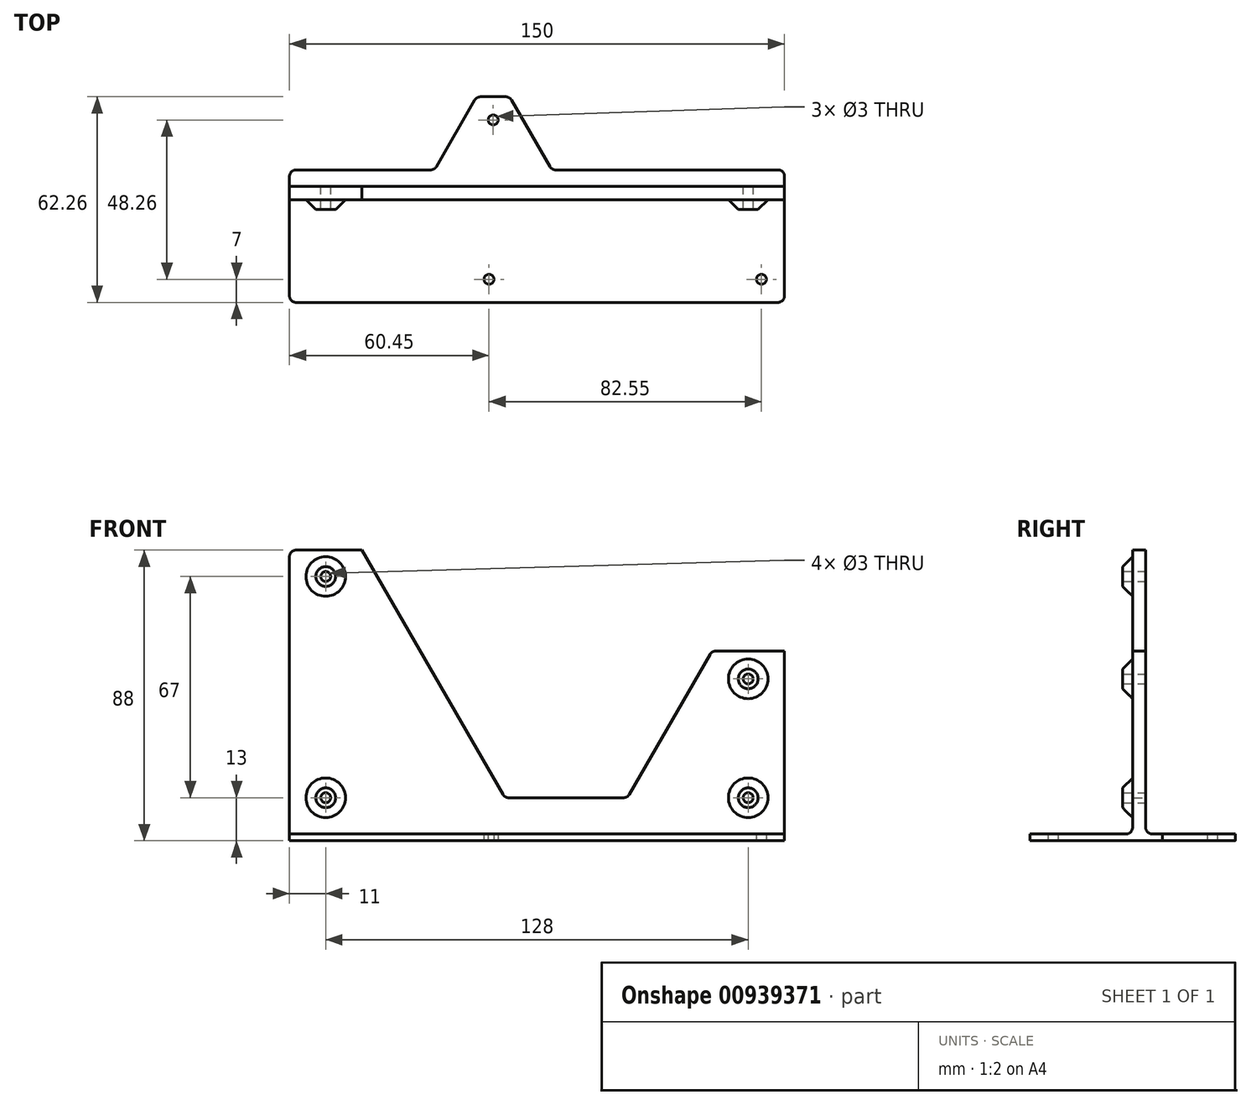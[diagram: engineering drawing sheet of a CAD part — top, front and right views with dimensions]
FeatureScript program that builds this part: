
annotation { "Feature Type Name" : "Feature", "Feature Type Description" : "" }
export const myFeature = defineFeature(function(context is Context, id is Id, definition is map)
    precondition{}
    {
        {
            var Q0;
            Q0=qCreatedBy(makeId("Top.planeOp"),FACE);
            var sketch = newSketch(context, id + "F0", { "sketchPlane" : qUnion([Q0])});
            skCircle(sketch, "E0", {"center": v(82.55, 0) * mm, "radius": 1.5 * mm});
            skCircle(sketch, "E1", {"center": v(1.27, 48.26) * mm, "radius": 1.5 * mm});
            skCircle(sketch, "E2", {"center": v(0, 0) * mm, "radius": 1.5 * mm});
            skLineSegment(sketch, "E3.bottom", {"start": v(-60.45, 55.26) * mm, "end": v(89.55, 55.26) * mm});
            skLineSegment(sketch, "E3.top", {"start": v(-60.45, -7) * mm, "end": v(89.55, -7) * mm});
            skLineSegment(sketch, "E3.left", {"start": v(-60.45, 55.26) * mm, "end": v(-60.45, -7) * mm});
            skLineSegment(sketch, "E3.right", {"start": v(89.55, 55.26) * mm, "end": v(89.55, -7) * mm});
            skLineSegment(sketch, "E4", {"start": v(-60.45, 28.13) * mm, "end": v(89.55, 28.13) * mm});
            skLineSegment(sketch, "E5", {"start": v(-60.45, 24.13) * mm, "end": v(89.55, 24.13) * mm});
            skLineSegment(sketch, "E6", {"start": v(6.27, 55.26) * mm, "end": v(19.05, 33.13) * mm});
            skLineSegment(sketch, "E7", {"start": v(19.05, 33.13) * mm, "end": v(89.55, 33.13) * mm});
            skLineSegment(sketch, "E8", {"start": v(-3.73, 55.26) * mm, "end": v(-16.5, 33.13) * mm});
            skLineSegment(sketch, "E9", {"start": v(-16.5, 33.13) * mm, "end": v(-60.45, 33.13) * mm});
            skSolve(sketch);
        }
        {
            var Q0;
            Q0=makeQuery(id+"F0.imprint","IMPRINT",FACE,{"disambiguationData":[TD([[makeQuery(id+"F0.imprint","IMPRINT",EDGE,{"derivedFrom":sQuery(id+"F0.wireOp",EDGE,"E1")}),-1.0]])]});
            var Q1;
            {var subQ0=sQuery(id+"F0.wireOp",EDGE,"E4");Q1=makeQuery(id+"F0.imprint","IMPRINT",FACE,{"disambiguationData":[TD([[makeQuery(id+"F0.imprint","IMPRINT",EDGE,{"derivedFrom":subQ0}),-1.0]])]});}
            var Q2;
            Q2=makeQuery(id+"F0.imprint","IMPRINT",FACE,{"disambiguationData":[TD([[makeQuery(id+"F0.imprint","IMPRINT",EDGE,{"derivedFrom":sQuery(id+"F0.wireOp",EDGE,"E0")}),-1.0]])]});
            extrude(context, id + "F1", {"entities" : qUnion([Q0, Q1, Q2]), "depth" : 2 * mm, "offsetDistance" : 25 * mm});
        }
        {
            var Q0;
            {var subQ0=sQuery(id+"F0.wireOp",EDGE,"E4");Q0=makeQuery(id+"F0.imprint","IMPRINT",FACE,{"disambiguationData":[TD([[makeQuery(id+"F0.imprint","IMPRINT",EDGE,{"derivedFrom":subQ0}),-1.0]])]});}
            extrude(context, id + "F2", {"entities" : qUnion([Q0]), "operationType" : NewBodyOperationType.ADD, "depth" : 88 * mm, "offsetDistance" : 25 * mm});
        }
        {
            var Q0;
            Q0=makeQuery(id+"F2.opExtrude","SWEPT_FACE",FACE,{"disambiguationData":[OSD([sQuery(id+"F0.wireOp",EDGE,"E5")])]});
            var sketch = newSketch(context, id + "F3", { "sketchPlane" : qUnion([Q0])});
            skCircle(sketch, "E10", {"center": v(-49.45, 80) * mm, "radius": 1.5 * mm});
            skCircle(sketch, "E11", {"center": v(-49.45, 13) * mm, "radius": 1.5 * mm});
            skCircle(sketch, "E12", {"center": v(78.55, 49) * mm, "radius": 1.5 * mm});
            skCircle(sketch, "E13", {"center": v(78.55, 13) * mm, "radius": 1.5 * mm});
            skLineSegment(sketch, "E14", {"start": v(-49.45, 80) * mm, "end": v(-49.45, 13) * mm, "construction": true});
            skLineSegment(sketch, "E15", {"start": v(-49.45, 13) * mm, "end": v(78.55, 13) * mm, "construction": true});
            skLineSegment(sketch, "E16", {"start": v(78.55, 13) * mm, "end": v(78.55, 49) * mm, "construction": true});
            skCircle(sketch, "E17", {"center": v(-49.45, 80) * mm, "radius": 6 * mm});
            skCircle(sketch, "E18", {"center": v(-49.45, 13) * mm, "radius": 6 * mm});
            skCircle(sketch, "E19", {"center": v(78.55, 49) * mm, "radius": 6 * mm});
            skCircle(sketch, "E20", {"center": v(78.55, 13) * mm, "radius": 6 * mm});
            skLineSegment(sketch, "E21", {"start": v(-38.45, 88) * mm, "end": v(4.85, 13) * mm});
            skLineSegment(sketch, "E22", {"start": v(4.85, 13) * mm, "end": v(41.91, 13) * mm});
            skLineSegment(sketch, "E23", {"start": v(41.91, 13) * mm, "end": v(67.55, 57.4) * mm});
            skLineSegment(sketch, "E24", {"start": v(67.55, 57.4) * mm, "end": v(89.55, 57.4) * mm});
            skSolve(sketch);
        }
        {
            var Q0;
            Q0=makeQuery(id+"F3.imprint","IMPRINT",FACE,{"disambiguationData":[TD([[makeQuery(id+"F3.imprint","IMPRINT",EDGE,{"derivedFrom":sQuery(id+"F3.wireOp",EDGE,"E10")}),1.0]])]});
            var Q1;
            Q1=makeQuery(id+"F3.imprint","IMPRINT",FACE,{"disambiguationData":[TD([[makeQuery(id+"F3.imprint","IMPRINT",EDGE,{"derivedFrom":sQuery(id+"F3.wireOp",EDGE,"E10")}),-1.0]])]});
            var Q2;
            Q2=makeQuery(id+"F3.imprint","IMPRINT",FACE,{"disambiguationData":[TD([[makeQuery(id+"F3.imprint","IMPRINT",EDGE,{"derivedFrom":sQuery(id+"F3.wireOp",EDGE,"E11")}),1.0]])]});
            var Q3;
            Q3=makeQuery(id+"F3.imprint","IMPRINT",FACE,{"disambiguationData":[TD([[makeQuery(id+"F3.imprint","IMPRINT",EDGE,{"derivedFrom":sQuery(id+"F3.wireOp",EDGE,"E11")}),-1.0]])]});
            var Q4;
            Q4=makeQuery(id+"F3.imprint","IMPRINT",FACE,{"disambiguationData":[TD([[makeQuery(id+"F3.imprint","IMPRINT",EDGE,{"derivedFrom":sQuery(id+"F3.wireOp",EDGE,"E13")}),1.0]])]});
            var Q5;
            Q5=makeQuery(id+"F3.imprint","IMPRINT",FACE,{"disambiguationData":[TD([[makeQuery(id+"F3.imprint","IMPRINT",EDGE,{"derivedFrom":sQuery(id+"F3.wireOp",EDGE,"E13")}),-1.0]])]});
            var Q6;
            Q6=makeQuery(id+"F3.imprint","IMPRINT",FACE,{"disambiguationData":[TD([[makeQuery(id+"F3.imprint","IMPRINT",EDGE,{"derivedFrom":sQuery(id+"F3.wireOp",EDGE,"E12")}),1.0]])]});
            var Q7;
            Q7=makeQuery(id+"F3.imprint","IMPRINT",FACE,{"disambiguationData":[TD([[makeQuery(id+"F3.imprint","IMPRINT",EDGE,{"derivedFrom":sQuery(id+"F3.wireOp",EDGE,"E12")}),-1.0]])]});
            extrude(context, id + "F4", {"entities" : qUnion([Q0, Q1, Q2, Q3, Q4, Q5, Q6, Q7]), "operationType" : NewBodyOperationType.ADD, "depth" : 3 * mm, "offsetDistance" : 25 * mm, "hasDraft" : true, "draftAngle" : 45 * degree, "draftPullDirection" : true});
        }
        {
            var Q0;
            Q0=makeQuery(id+"F3.imprint","IMPRINT",FACE,{"disambiguationData":[TD([[makeQuery(id+"F3.imprint","IMPRINT",EDGE,{"derivedFrom":sQuery(id+"F3.wireOp",EDGE,"E11")}),1.0]])]});
            var Q1;
            Q1=makeQuery(id+"F3.imprint","IMPRINT",FACE,{"disambiguationData":[TD([[makeQuery(id+"F3.imprint","IMPRINT",EDGE,{"derivedFrom":sQuery(id+"F3.wireOp",EDGE,"E13")}),1.0]])]});
            var Q2;
            Q2=makeQuery(id+"F3.imprint","IMPRINT",FACE,{"disambiguationData":[TD([[makeQuery(id+"F3.imprint","IMPRINT",EDGE,{"derivedFrom":sQuery(id+"F3.wireOp",EDGE,"E12")}),1.0]])]});
            var Q3;
            Q3=makeQuery(id+"F3.imprint","IMPRINT",FACE,{"disambiguationData":[TD([[makeQuery(id+"F3.imprint","IMPRINT",EDGE,{"derivedFrom":sQuery(id+"F3.wireOp",EDGE,"E10")}),1.0]])]});
            var Q4;
            {var subQ1=sQuery(id+"F3.wireOp",EDGE,"E21");Q4=makeQuery(id+"F3.imprint","IMPRINT",FACE,{"disambiguationData":[TD([[makeQuery(id+"F3.imprint","IMPRINT",EDGE,{"derivedFrom":subQ1}),1.0]])]});}
            extrude(context, id + "F5", {"entities" : qUnion([Q0, Q1, Q2, Q3, Q4]), "operationType" : NewBodyOperationType.REMOVE, "endBound" : BoundingType.THROUGH_ALL, "depth" : 25 * mm, "offsetDistance" : 25 * mm, "hasSecondDirection" : true, "secondDirectionBound" : SecondDirectionBoundingType.THROUGH_ALL, "secondDirectionOppositeDirection" : true, "secondDirectionDepth" : 25 * mm});
        }
        {
            var Q0;
            Q0=makeQuery(id+"F2.opExtrude","CAP_EDGE",EDGE,{"disambiguationData":[OSD([sQuery(id+"F0.wireOp",EDGE,"E3.left")])],"isStart":false});
            var Q1;
            Q1=makeQuery(id+"F5.boolean.opBoolean","COPY",EDGE,{"derivedFrom":makeQuery(id+"F5.opExtrude","SWEPT_EDGE",EDGE,{"disambiguationData":[OSD([sQuery(id+"F0.wireOp",EDGE,"E5"),sQuery(id+"F3.wireOp",EDGE,"E21")])]})});
            var Q2;
            Q2=makeQuery(id+"F5.boolean.opBoolean","COPY",EDGE,{"derivedFrom":makeQuery(id+"F5.opExtrude","SWEPT_EDGE",EDGE,{"disambiguationData":[OSD([sQuery(id+"F3.wireOp",EDGE,"E21"),sQuery(id+"F3.wireOp",EDGE,"E22")])]})});
            var Q3;
            Q3=makeQuery(id+"F5.boolean.opBoolean","COPY",EDGE,{"derivedFrom":makeQuery(id+"F5.opExtrude","SWEPT_EDGE",EDGE,{"disambiguationData":[OSD([sQuery(id+"F3.wireOp",EDGE,"E22"),sQuery(id+"F3.wireOp",EDGE,"E23")])]})});
            var Q4;
            Q4=makeQuery(id+"F5.boolean.opBoolean","COPY",EDGE,{"derivedFrom":makeQuery(id+"F5.opExtrude","SWEPT_EDGE",EDGE,{"disambiguationData":[OSD([sQuery(id+"F3.wireOp",EDGE,"E23"),sQuery(id+"F3.wireOp",EDGE,"E24")])]})});
            var Q5;
            Q5=makeQuery(id+"F5.boolean.opBoolean","COPY",EDGE,{"derivedFrom":makeQuery(id+"F5.opExtrude","SWEPT_EDGE",EDGE,{"disambiguationData":[OSD([sQuery(id+"F0.wireOp",EDGE,"E3.right"),sQuery(id+"F0.wireOp",EDGE,"E5"),sQuery(id+"F3.wireOp",EDGE,"E24")])]})});
            var Q6;
            Q6=makeQuery(id+"F1.opExtrude","SWEPT_EDGE",EDGE,{"disambiguationData":[OSD([sQuery(id+"F0.wireOp",EDGE,"E3.top"),sQuery(id+"F0.wireOp",EDGE,"E3.right")])]});
            var Q7;
            Q7=makeQuery(id+"F1.opExtrude","SWEPT_EDGE",EDGE,{"disambiguationData":[OSD([sQuery(id+"F0.wireOp",EDGE,"E3.right"),sQuery(id+"F0.wireOp",EDGE,"E7")])]});
            var Q8;
            Q8=makeQuery(id+"F1.opExtrude","SWEPT_EDGE",EDGE,{"disambiguationData":[OSD([sQuery(id+"F0.wireOp",EDGE,"E6"),sQuery(id+"F0.wireOp",EDGE,"E7")])]});
            var Q9;
            Q9=makeQuery(id+"F1.opExtrude","SWEPT_EDGE",EDGE,{"disambiguationData":[OSD([sQuery(id+"F0.wireOp",EDGE,"E3.bottom"),sQuery(id+"F0.wireOp",EDGE,"E6")])]});
            var Q10;
            Q10=makeQuery(id+"F1.opExtrude","SWEPT_EDGE",EDGE,{"disambiguationData":[OSD([sQuery(id+"F0.wireOp",EDGE,"E3.bottom"),sQuery(id+"F0.wireOp",EDGE,"E8")])]});
            var Q11;
            Q11=makeQuery(id+"F1.opExtrude","SWEPT_EDGE",EDGE,{"disambiguationData":[OSD([sQuery(id+"F0.wireOp",EDGE,"E8"),sQuery(id+"F0.wireOp",EDGE,"E9")])]});
            var Q12;
            Q12=makeQuery(id+"F1.opExtrude","SWEPT_EDGE",EDGE,{"disambiguationData":[OSD([sQuery(id+"F0.wireOp",EDGE,"E3.left"),sQuery(id+"F0.wireOp",EDGE,"E9")])]});
            var Q13;
            Q13=makeQuery(id+"F1.opExtrude","SWEPT_EDGE",EDGE,{"disambiguationData":[OSD([sQuery(id+"F0.wireOp",EDGE,"E3.top"),sQuery(id+"F0.wireOp",EDGE,"E3.left")])]});
            var Q14;
            Q14=makeQuery(id+"F2.boolean.opBoolean","INTERSECT",EDGE,{"derivedFrom":[makeQuery(id+"F1.opExtrude","CAP_FACE",FACE,{"disambiguationData":[OSD([sQuery(id+"F0.wireOp",EDGE,"E0"),sQuery(id+"F0.wireOp",EDGE,"E1"),sQuery(id+"F0.wireOp",EDGE,"E2"),sQuery(id+"F0.wireOp",EDGE,"E3.bottom"),sQuery(id+"F0.wireOp",EDGE,"E3.top"),sQuery(id+"F0.wireOp",EDGE,"E3.left"),sQuery(id+"F0.wireOp",EDGE,"E3.right"),sQuery(id+"F0.wireOp",EDGE,"E6"),sQuery(id+"F0.wireOp",EDGE,"E7"),sQuery(id+"F0.wireOp",EDGE,"E8"),sQuery(id+"F0.wireOp",EDGE,"E9")])],"isStart":false}),makeQuery(id+"F2.opExtrude","SWEPT_FACE",FACE,{"disambiguationData":[OSD([sQuery(id+"F0.wireOp",EDGE,"E5")])]})]});
            var Q15;
            Q15=makeQuery(id+"F2.boolean.opBoolean","INTERSECT",EDGE,{"derivedFrom":[makeQuery(id+"F1.opExtrude","CAP_FACE",FACE,{"disambiguationData":[OSD([sQuery(id+"F0.wireOp",EDGE,"E0"),sQuery(id+"F0.wireOp",EDGE,"E1"),sQuery(id+"F0.wireOp",EDGE,"E2"),sQuery(id+"F0.wireOp",EDGE,"E3.bottom"),sQuery(id+"F0.wireOp",EDGE,"E3.top"),sQuery(id+"F0.wireOp",EDGE,"E3.left"),sQuery(id+"F0.wireOp",EDGE,"E3.right"),sQuery(id+"F0.wireOp",EDGE,"E6"),sQuery(id+"F0.wireOp",EDGE,"E7"),sQuery(id+"F0.wireOp",EDGE,"E8"),sQuery(id+"F0.wireOp",EDGE,"E9")])],"isStart":false}),makeQuery(id+"F2.opExtrude","SWEPT_FACE",FACE,{"disambiguationData":[OSD([sQuery(id+"F0.wireOp",EDGE,"E4")])]})]});
            fillet(context, id + "F6", {"entities" : qUnion([Q0, Q1, Q2, Q3, Q4, Q5, Q6, Q7, Q8, Q9, Q10, Q11, Q12, Q13, Q14, Q15]), "radius" : 2 * mm, "allowEdgeOverflow" : false});
        }
    });
